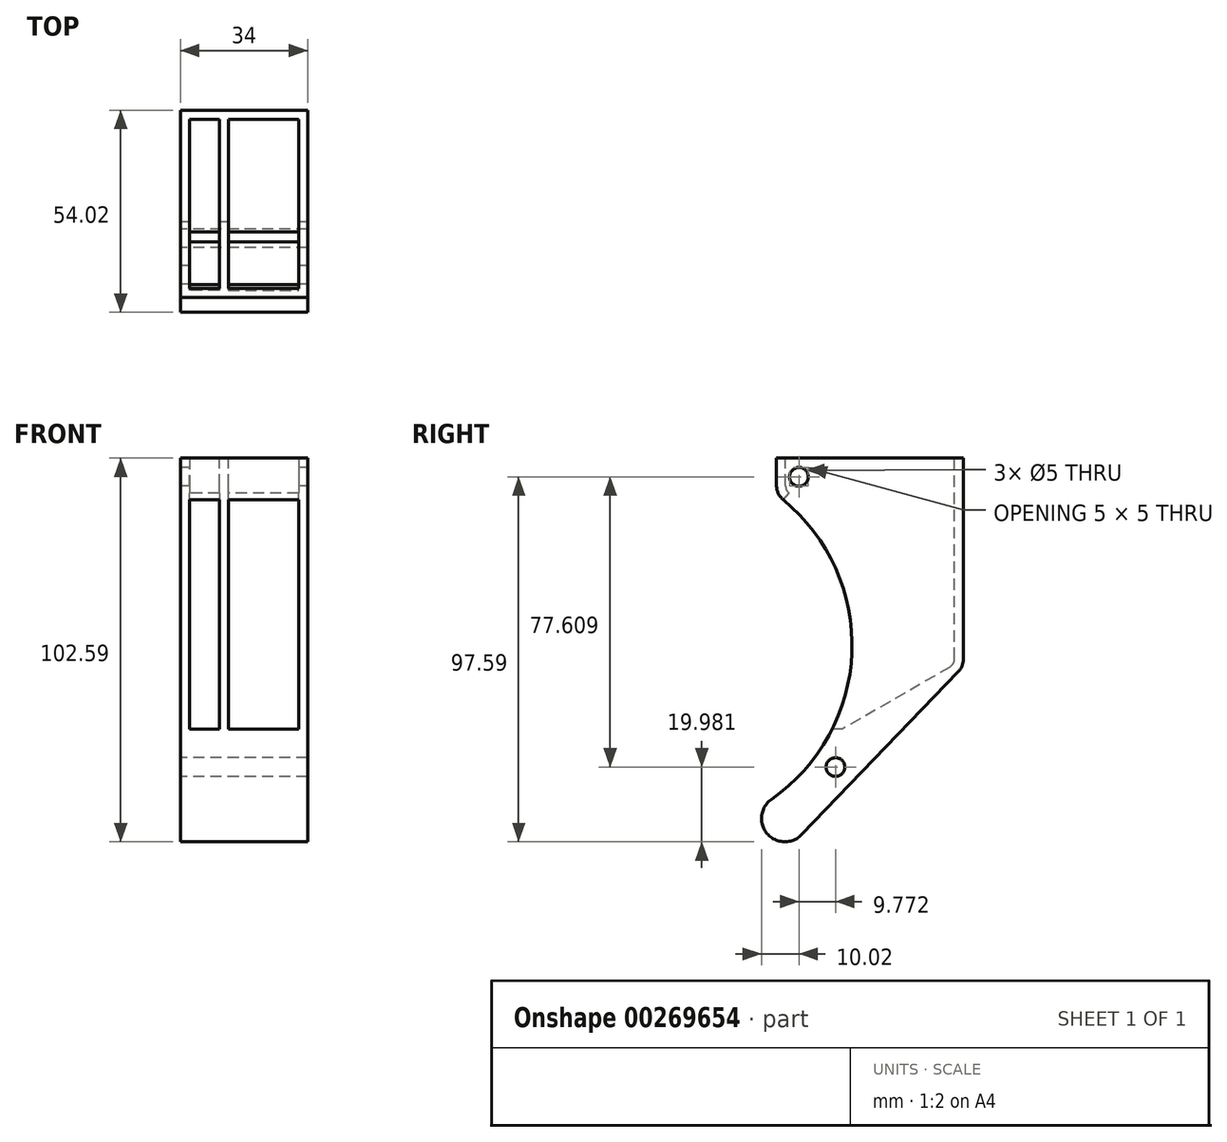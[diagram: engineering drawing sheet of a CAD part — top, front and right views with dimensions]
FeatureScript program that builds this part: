
annotation { "Feature Type Name" : "Feature", "Feature Type Description" : "" }
export const myFeature = defineFeature(function(context is Context, id is Id, definition is map)
    precondition{}
    {
        {
            var Q0;
            Q0=qCreatedBy(makeId("Right.planeOp"),FACE);
            var sketch = newSketch(context, id + "F0", { "sketchPlane" : qUnion([Q0])});
            skLineSegment(sketch, "E0", {"start": v(50, -56.54) * mm, "end": v(50, 0) * mm});
            skLineSegment(sketch, "E1", {"start": v(50, 0) * mm, "end": v(0, 0) * mm});
            skArc(sketch, "E2", {"start": v(10.89, -79.13) * mm, "mid": v(19.6, -42.22) * mm, "end": v(0, -9.75) * mm});
            skLineSegment(sketch, "E3", {"start": v(0, 0) * mm, "end": v(0, -9.75) * mm});
            skLineSegment(sketch, "E4", {"start": v(50, -56.54) * mm, "end": v(10.89, -79.13) * mm});
            skCircle(sketch, "E5", {"center": v(-30, -50) * mm, "radius": 50.2 * mm, "construction": true});
            skSolve(sketch);
        }
        {
            var Q0;
            Q0=qSketchRegion(id+"F0",true);
            extrude(context, id + "F1", {"entities" : qUnion([Q0]), "depth" : 34 * mm});
        }
        {
            var Q0;
            Q0=makeQuery(id+"F1.opExtrude","SWEPT_EDGE",EDGE,{"disambiguationData":[OSD([sQuery(id+"F0.wireOp",EDGE,"E0"),sQuery(id+"F0.wireOp",EDGE,"E4")])]});
            var Q1;
            Q1=makeQuery(id+"F1.opExtrude","SWEPT_EDGE",EDGE,{"disambiguationData":[OSD([sQuery(id+"F0.wireOp",EDGE,"E2"),sQuery(id+"F0.wireOp",EDGE,"E3")])]});
            fillet(context, id + "F2", {"entities" : qUnion([Q0, Q1]), "radius" : 5 * mm, "tangentPropagation" : true, "allowEdgeOverflow" : false});
        }
        {
            var Q0;
            Q0=makeQuery(id+"F1.opExtrude","SWEPT_FACE",FACE,{"disambiguationData":[OSD([sQuery(id+"F0.wireOp",EDGE,"E1")])]});
            shell(context, id + "F3", {"entities" : qUnion([Q0]), "thickness" : 2.4 * mm});
        }
        {
            var Q0;
            Q0=makeQuery(id+"F1.opExtrude","SWEPT_FACE",FACE,{"disambiguationData":[OSD([sQuery(id+"F0.wireOp",EDGE,"E1")])]});
            var sketch = newSketch(context, id + "F4", { "sketchPlane" : qUnion([Q0])});
            skLineSegment(sketch, "E6.bottom", {"start": v(10.4, 47.6) * mm, "end": v(12.8, 47.6) * mm});
            skLineSegment(sketch, "E6.top", {"start": v(10.4, 2.4) * mm, "end": v(12.8, 2.4) * mm});
            skLineSegment(sketch, "E6.left", {"start": v(10.4, 47.6) * mm, "end": v(10.4, 2.4) * mm});
            skLineSegment(sketch, "E6.right", {"start": v(12.8, 47.6) * mm, "end": v(12.8, 2.4) * mm});
            skSolve(sketch);
        }
        {
            var Q0;
            Q0=qSketchRegion(id+"F4",true);
            extrude(context, id + "F5", {"entities" : qUnion([Q0]), "operationType" : NewBodyOperationType.ADD, "endBound" : BoundingType.UP_TO_NEXT, "oppositeDirection" : true, "depth" : 25 * mm});
        }
        {
            var Q0;
            Q0=makeQuery(id+"F1.opExtrude","CAP_FACE",FACE,{"disambiguationData":[OSD([sQuery(id+"F0.wireOp",EDGE,"E0"),sQuery(id+"F0.wireOp",EDGE,"E1"),sQuery(id+"F0.wireOp",EDGE,"E2"),sQuery(id+"F0.wireOp",EDGE,"E3"),sQuery(id+"F0.wireOp",EDGE,"E4")])],"isStart":true});
            var sketch = newSketch(context, id + "F6", { "sketchPlane" : qUnion([Q0])});
            skArc(sketch, "E7", {"start": v(-20.1, -86.77) * mm, "mid": v(-11.94, -87.23) * mm, "end": v(-10.89, -79.13) * mm});
            skCircle(sketch, "E8", {"center": v(-15.77, -82.6) * mm, "radius": 2.5 * mm});
            skLineSegment(sketch, "E9.0", {"start": v(-47.5, -57.99) * mm, "end": v(-10.89, -79.13) * mm});
            skArc(sketch, "E9.1", {"start": v(-48.6, -57.12) * mm, "mid": v(-48.08, -57.6) * mm, "end": v(-47.5, -57.99) * mm});
            skLineSegment(sketch, "E10", {"start": v(-20.1, -86.77) * mm, "end": v(-48.6, -57.12) * mm});
            skSolve(sketch);
        }
        {
            var Q0;
            Q0=qSketchRegion(id+"F6",true);
            var Q1;
            Q1=makeQuery(id+"F1.opExtrude","CAP_FACE",FACE,{"disambiguationData":[OSD([sQuery(id+"F0.wireOp",EDGE,"E0"),sQuery(id+"F0.wireOp",EDGE,"E1"),sQuery(id+"F0.wireOp",EDGE,"E2"),sQuery(id+"F0.wireOp",EDGE,"E3"),sQuery(id+"F0.wireOp",EDGE,"E4")])],"isStart":false});
            extrude(context, id + "F7", {"entities" : qUnion([Q0]), "operationType" : NewBodyOperationType.ADD, "endBound" : BoundingType.UP_TO_SURFACE, "oppositeDirection" : true, "endBoundEntityFace" : qUnion([Q1]), "depth" : 25 * mm});
        }
        {
            var Q0;
            Q0=makeQuery(id+"F7.boolean.opBoolean","MERGE",FACE,{"derivedFrom":[makeQuery(id+"F1.opExtrude","CAP_FACE",FACE,{"disambiguationData":[OSD([sQuery(id+"F0.wireOp",EDGE,"E0"),sQuery(id+"F0.wireOp",EDGE,"E1"),sQuery(id+"F0.wireOp",EDGE,"E2"),sQuery(id+"F0.wireOp",EDGE,"E3"),sQuery(id+"F0.wireOp",EDGE,"E4")])],"isStart":true}),makeQuery(id+"F7.opExtrude","CAP_FACE",FACE,{"disambiguationData":[OSD([sQuery(id+"F6.wireOp",EDGE,"E7"),sQuery(id+"F6.wireOp",EDGE,"E8"),sQuery(id+"F6.wireOp",EDGE,"E9.0"),sQuery(id+"F6.wireOp",EDGE,"E9.1"),sQuery(id+"F6.wireOp",EDGE,"E10")])],"isStart":true})]});
            var sketch = newSketch(context, id + "F8", { "sketchPlane" : qUnion([Q0])});
            skLineSegment(sketch, "E11", {"start": v(-20.1, -86.77) * mm, "end": v(-6.72, -100.67) * mm});
            skArc(sketch, "E12", {"start": v(-10.89, -79.13) * mm, "mid": v(-5.3, -85.7) * mm, "end": v(1.34, -91.22) * mm});
            skArc(sketch, "E13", {"start": v(-6.72, -100.67) * mm, "mid": v(2.53, -100.4) * mm, "end": v(1.34, -91.22) * mm});
            skArc(sketch, "E14.0", {"start": v(-20.1, -86.77) * mm, "mid": v(-11.94, -87.23) * mm, "end": v(-10.89, -79.13) * mm});
            skSolve(sketch);
        }
        {
            var Q0;
            Q0=qSketchRegion(id+"F8",true);
            var Q1;
            {var subQ0=sQuery(id+"F0.wireOp",EDGE,"E4");var subQ1=sQuery(id+"F0.wireOp",EDGE,"E3");var subQ2=sQuery(id+"F0.wireOp",EDGE,"E2");var subQ3=sQuery(id+"F0.wireOp",EDGE,"E1");var subQ4=sQuery(id+"F0.wireOp",EDGE,"E0");Q1=makeQuery(id+"F7.boolean.opBoolean","MERGE",FACE,{"derivedFrom":[makeQuery(id+"F1.opExtrude","CAP_FACE",FACE,{"disambiguationData":[OSD([subQ4,subQ3,subQ2,subQ1,subQ0])],"isStart":false}),makeQuery(id+"F7.opExtrude","CAP_FACE",FACE,{"disambiguationData":[OSD([subQ4,subQ3,subQ2,subQ1,subQ0])],"isStart":false})]});}
            extrude(context, id + "F9", {"entities" : qUnion([Q0]), "operationType" : NewBodyOperationType.ADD, "endBound" : BoundingType.UP_TO_SURFACE, "oppositeDirection" : true, "endBoundEntityFace" : qUnion([Q1]), "depth" : 25 * mm});
        }
        {
            var Q0;
            Q0=makeQuery(id+"F1.opExtrude","CAP_FACE",FACE,{"disambiguationData":[OSD([sQuery(id+"F0.wireOp",EDGE,"E0"),sQuery(id+"F0.wireOp",EDGE,"E1"),sQuery(id+"F0.wireOp",EDGE,"E2"),sQuery(id+"F0.wireOp",EDGE,"E3"),sQuery(id+"F0.wireOp",EDGE,"E4")])],"isStart":true});
            var sketch = newSketch(context, id + "F10", { "sketchPlane" : qUnion([Q0])});
            skCircle(sketch, "E15", {"center": v(-6, -5) * mm, "radius": 2.5 * mm});
            skSolve(sketch);
        }
        {
            var Q0;
            Q0=qSketchRegion(id+"F10",true);
            var Q1;
            {var subQ0=sQuery(id+"F0.wireOp",EDGE,"E4");var subQ1=sQuery(id+"F0.wireOp",EDGE,"E3");var subQ2=sQuery(id+"F0.wireOp",EDGE,"E2");var subQ3=sQuery(id+"F0.wireOp",EDGE,"E1");var subQ4=sQuery(id+"F0.wireOp",EDGE,"E0");Q1=makeQuery(id+"F3.opShell","OFFSET_FACE",FACE,{"disambiguationData":[OSD([subQ4,subQ3,subQ2,subQ1,subQ0]),TDD([makeQuery(id+"F1.opExtrude","CAP_FACE",FACE,{"disambiguationData":[OSD([subQ4,subQ3,subQ2,subQ1,subQ0])],"isStart":true})])]});}
            extrude(context, id + "F11", {"entities" : qUnion([Q0]), "operationType" : NewBodyOperationType.REMOVE, "endBound" : BoundingType.UP_TO_SURFACE, "oppositeDirection" : true, "endBoundEntityFace" : qUnion([Q1]), "depth" : 25 * mm});
        }
        {
            var Q0;
            {var subQ0=sQuery(id+"F0.wireOp",EDGE,"E4");var subQ1=sQuery(id+"F0.wireOp",EDGE,"E3");var subQ2=sQuery(id+"F0.wireOp",EDGE,"E2");var subQ3=sQuery(id+"F0.wireOp",EDGE,"E1");var subQ4=sQuery(id+"F0.wireOp",EDGE,"E0");Q0=makeQuery(id+"F3.opShell","OFFSET_FACE",FACE,{"disambiguationData":[OSD([subQ4,subQ3,subQ2,subQ1,subQ0]),TDD([makeQuery(id+"F1.opExtrude","CAP_FACE",FACE,{"disambiguationData":[OSD([subQ4,subQ3,subQ2,subQ1,subQ0])],"isStart":false})])]});}
            var sketch = newSketch(context, id + "F12", { "sketchPlane" : qUnion([Q0])});
            skCircle(sketch, "E16.0", {"center": v(-6, -5) * mm, "radius": 2.5 * mm});
            skSolve(sketch);
        }
        {
            var Q0;
            Q0=makeQuery(id+"F12.imprint","IMPRINT",FACE,{"disambiguationData":[TD([[makeQuery(id+"F12.imprint","IMPRINT",EDGE,{"derivedFrom":sQuery(id+"F12.wireOp",EDGE,"E16.0")}),1.0]])]});
            extrude(context, id + "F13", {"entities" : qUnion([Q0]), "operationType" : NewBodyOperationType.REMOVE, "endBound" : BoundingType.THROUGH_ALL, "oppositeDirection" : true, "depth" : 25 * mm});
        }
        {
            var Q0;
            {var subQ0=sQuery(id+"F0.wireOp",EDGE,"E4");var subQ1=sQuery(id+"F0.wireOp",EDGE,"E3");var subQ2=sQuery(id+"F0.wireOp",EDGE,"E2");var subQ3=sQuery(id+"F0.wireOp",EDGE,"E1");var subQ4=sQuery(id+"F0.wireOp",EDGE,"E0");Q0=makeQuery(id+"F3.opShell","OFFSET_FACE",FACE,{"disambiguationData":[OSD([subQ4,subQ3,subQ2,subQ1,subQ0]),TDD([makeQuery(id+"F1.opExtrude","CAP_FACE",FACE,{"disambiguationData":[OSD([subQ4,subQ3,subQ2,subQ1,subQ0])],"isStart":false})])]});}
            var sketch = newSketch(context, id + "F14", { "sketchPlane" : qUnion([Q0])});
            skArc(sketch, "E17.0", {"start": v(-17.54, -72.52) * mm, "mid": v(-21.32, -38.48) * mm, "end": v(-3.35, -9.33) * mm});
            skArc(sketch, "E18.0", {"start": v(-14.87, -72.52) * mm, "mid": v(-19.1, -39.56) * mm, "end": v(-1.83, -11.18) * mm});
            skLineSegment(sketch, "E19", {"start": v(-17.54, -72.52) * mm, "end": v(-14.87, -72.52) * mm});
            skLineSegment(sketch, "E20", {"start": v(-1.83, -11.18) * mm, "end": v(-3.35, -9.33) * mm});
            skSolve(sketch);
        }
        {
            var Q0;
            Q0=qSketchRegion(id+"F14",true);
            var Q1;
            Q1=makeQuery(id+"F5.opExtrude","SWEPT_FACE",FACE,{"disambiguationData":[OSD([sQuery(id+"F4.wireOp",EDGE,"E6.right")])]});
            extrude(context, id + "F15", {"entities" : qUnion([Q0]), "operationType" : NewBodyOperationType.REMOVE, "endBound" : BoundingType.UP_TO_SURFACE, "endBoundEntityFace" : qUnion([Q1]), "depth" : 25 * mm});
        }
        {
            var Q0;
            {var subQ0=sQuery(id+"F0.wireOp",EDGE,"E4");var subQ1=sQuery(id+"F0.wireOp",EDGE,"E3");var subQ2=sQuery(id+"F0.wireOp",EDGE,"E2");var subQ3=sQuery(id+"F0.wireOp",EDGE,"E1");var subQ4=sQuery(id+"F0.wireOp",EDGE,"E0");Q0=makeQuery(id+"F3.opShell","OFFSET_FACE",FACE,{"disambiguationData":[OSD([subQ4,subQ3,subQ2,subQ1,subQ0]),TDD([makeQuery(id+"F1.opExtrude","CAP_FACE",FACE,{"disambiguationData":[OSD([subQ4,subQ3,subQ2,subQ1,subQ0])],"isStart":true})])]});}
            var sketch = newSketch(context, id + "F16", { "sketchPlane" : qUnion([Q0])});
            skArc(sketch, "E21.0", {"start": v(17.54, -72.52) * mm, "mid": v(21.32, -38.48) * mm, "end": v(3.35, -9.33) * mm});
            skLineSegment(sketch, "E21.1", {"start": v(17.54, -72.52) * mm, "end": v(14.87, -72.52) * mm});
            skArc(sketch, "E21.2", {"start": v(14.87, -72.52) * mm, "mid": v(19.1, -39.56) * mm, "end": v(1.83, -11.18) * mm});
            skLineSegment(sketch, "E21.3", {"start": v(1.83, -11.18) * mm, "end": v(3.35, -9.33) * mm});
            skSolve(sketch);
        }
        {
            var Q0;
            Q0=qSketchRegion(id+"F16",true);
            var Q1;
            Q1=makeQuery(id+"F5.opExtrude","SWEPT_FACE",FACE,{"disambiguationData":[OSD([sQuery(id+"F4.wireOp",EDGE,"E6.left")])]});
            extrude(context, id + "F17", {"entities" : qUnion([Q0]), "operationType" : NewBodyOperationType.REMOVE, "endBound" : BoundingType.UP_TO_SURFACE, "endBoundEntityFace" : qUnion([Q1]), "depth" : 25 * mm});
        }
    });
